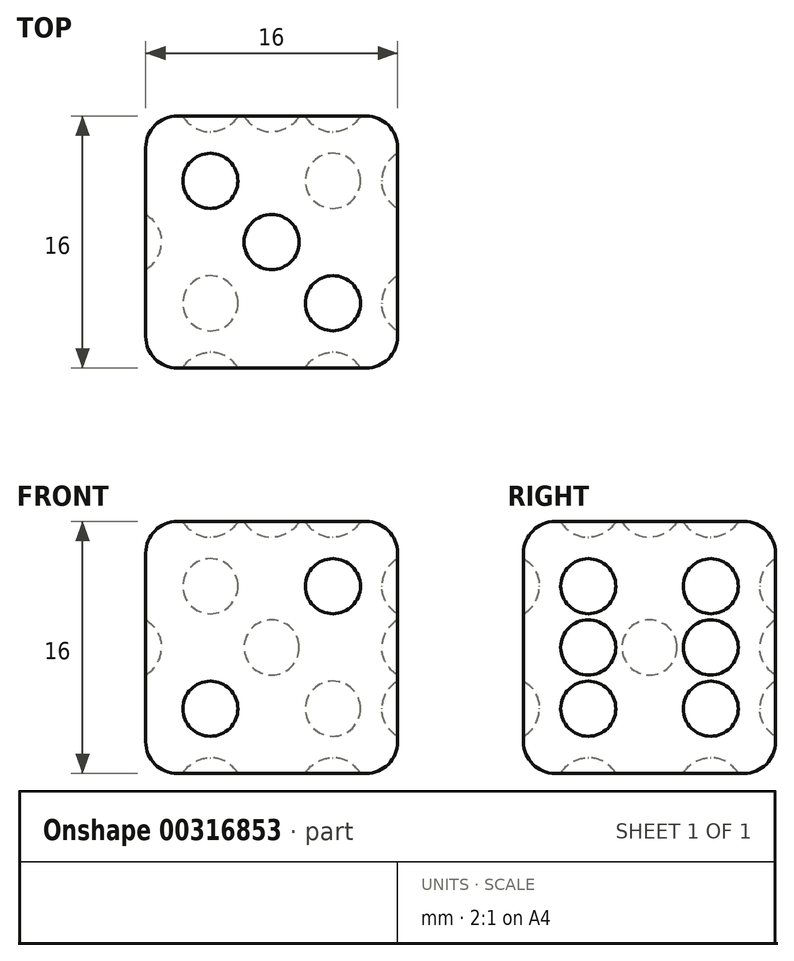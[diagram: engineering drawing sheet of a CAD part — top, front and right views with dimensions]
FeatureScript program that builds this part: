
annotation { "Feature Type Name" : "Feature", "Feature Type Description" : "" }
export const myFeature = defineFeature(function(context is Context, id is Id, definition is map)
    precondition{}
    {
        {
            var Q0;
            Q0=qCreatedBy(makeId("Top.planeOp"),FACE);
            var sketch = newSketch(context, id + "F0", { "sketchPlane" : qUnion([Q0])});
            skLineSegment(sketch, "E0.bottom", {"start": v(-8, 8) * mm, "end": v(8, 8) * mm});
            skLineSegment(sketch, "E0.top", {"start": v(-8, -8) * mm, "end": v(8, -8) * mm});
            skLineSegment(sketch, "E0.left", {"start": v(-8, 8) * mm, "end": v(-8, -8) * mm});
            skLineSegment(sketch, "E0.right", {"start": v(8, 8) * mm, "end": v(8, -8) * mm});
            skPoint(sketch, "E0.middle", {"position": v(0, 0) * mm});
            skSolve(sketch);
        }
        {
            var Q0;
            Q0=makeQuery(id+"F0.imprint","IMPRINT",FACE,{"disambiguationData":[TD([[makeQuery(id+"F0.imprint","IMPRINT",EDGE,{"derivedFrom":sQuery(id+"F0.wireOp",EDGE,"E0.bottom")}),-1.0]])]});
            extrude(context, id + "F1", {"entities" : qUnion([Q0]), "oppositeDirection" : true, "depth" : 16 * mm});
        }
        {
            var Q0;
            Q0=makeQuery(id+"F1.opExtrude","CAP_EDGE",EDGE,{"disambiguationData":[OSD([sQuery(id+"F0.wireOp",EDGE,"E0.top")])],"isStart":true});
            var Q1;
            Q1=makeQuery(id+"F1.opExtrude","CAP_EDGE",EDGE,{"disambiguationData":[OSD([sQuery(id+"F0.wireOp",EDGE,"E0.left")])],"isStart":true});
            var Q2;
            Q2=makeQuery(id+"F1.opExtrude","CAP_EDGE",EDGE,{"disambiguationData":[OSD([sQuery(id+"F0.wireOp",EDGE,"E0.bottom")])],"isStart":true});
            var Q3;
            Q3=makeQuery(id+"F1.opExtrude","CAP_EDGE",EDGE,{"disambiguationData":[OSD([sQuery(id+"F0.wireOp",EDGE,"E0.right")])],"isStart":true});
            var Q4;
            Q4=makeQuery(id+"F1.opExtrude","SWEPT_EDGE",EDGE,{"disambiguationData":[OSD([sQuery(id+"F0.wireOp",EDGE,"E0.top"),sQuery(id+"F0.wireOp",EDGE,"E0.right")])]});
            var Q5;
            Q5=makeQuery(id+"F1.opExtrude","SWEPT_EDGE",EDGE,{"disambiguationData":[OSD([sQuery(id+"F0.wireOp",EDGE,"E0.bottom"),sQuery(id+"F0.wireOp",EDGE,"E0.right")])]});
            var Q6;
            Q6=makeQuery(id+"F1.opExtrude","CAP_EDGE",EDGE,{"disambiguationData":[OSD([sQuery(id+"F0.wireOp",EDGE,"E0.right")])],"isStart":false});
            var Q7;
            Q7=makeQuery(id+"F1.opExtrude","CAP_EDGE",EDGE,{"disambiguationData":[OSD([sQuery(id+"F0.wireOp",EDGE,"E0.bottom")])],"isStart":false});
            var Q8;
            Q8=makeQuery(id+"F1.opExtrude","SWEPT_EDGE",EDGE,{"disambiguationData":[OSD([sQuery(id+"F0.wireOp",EDGE,"E0.bottom"),sQuery(id+"F0.wireOp",EDGE,"E0.left")])]});
            var Q9;
            Q9=makeQuery(id+"F1.opExtrude","CAP_EDGE",EDGE,{"disambiguationData":[OSD([sQuery(id+"F0.wireOp",EDGE,"E0.left")])],"isStart":false});
            var Q10;
            Q10=makeQuery(id+"F1.opExtrude","SWEPT_EDGE",EDGE,{"disambiguationData":[OSD([sQuery(id+"F0.wireOp",EDGE,"E0.top"),sQuery(id+"F0.wireOp",EDGE,"E0.left")])]});
            var Q11;
            Q11=makeQuery(id+"F1.opExtrude","CAP_EDGE",EDGE,{"disambiguationData":[OSD([sQuery(id+"F0.wireOp",EDGE,"E0.top")])],"isStart":false});
            var Q12;
            Q12=makeQuery(id+"F1.opExtrude","SWEPT_FACE",FACE,{"disambiguationData":[OSD([sQuery(id+"F0.wireOp",EDGE,"E0.bottom")])]});
            fillet(context, id + "F2", {"entities" : qUnion([Q0, Q1, Q2, Q3, Q4, Q5, Q6, Q7, Q8, Q9, Q10, Q11, Q12]), "radius" : 2 * mm, "tangentPropagation" : true, "allowEdgeOverflow" : false});
        }
        {
            var Q0;
            Q0=makeQuery(id+"F1.opExtrude","CAP_FACE",FACE,{"disambiguationData":[OSD([sQuery(id+"F0.wireOp",EDGE,"E0.bottom"),sQuery(id+"F0.wireOp",EDGE,"E0.top"),sQuery(id+"F0.wireOp",EDGE,"E0.left"),sQuery(id+"F0.wireOp",EDGE,"E0.right")])],"isStart":true});
            var sketch = newSketch(context, id + "F3", { "sketchPlane" : qUnion([Q0])});
            skCircle(sketch, "E1", {"center": v(0, 0) * mm, "radius": 1.75 * mm});
            skCircle(sketch, "E2", {"center": v(3.89, -3.89) * mm, "radius": 1.75 * mm});
            skPoint(sketch, "E2.second.point", {"position": v(3.96, -5.64) * mm});
            skCircle(sketch, "E3", {"center": v(-3.9, 3.89) * mm, "radius": 1.75 * mm});
            skPoint(sketch, "E3.third.point", {"position": v(-4.7, 2.34) * mm});
            skSolve(sketch);
        }
        {
            var Q0;
            Q0 = qSketchRegion(id + "F3", true);
            extrude(context, id + "F4", {"entities" : qUnion([Q0]), "operationType" : NewBodyOperationType.REMOVE, "oppositeDirection" : true, "depth" : 1 * mm});
        }
        {
            var Q0;
            Q0=makeQuery(id+"F4.boolean.opBoolean","COPY",EDGE,{"derivedFrom":makeQuery(id+"F4.opExtrude","CAP_EDGE",EDGE,{"disambiguationData":[OSD([sQuery(id+"F3.wireOp",EDGE,"E2")])],"isStart":false})});
            fillet(context, id + "F5", {"entities" : qUnion([Q0]), "radius" : 2.02 * mm, "tangentPropagation" : true, "allowEdgeOverflow" : false});
        }
        {
            var Q0;
            Q0=makeQuery(id+"F4.boolean.opBoolean","COPY",EDGE,{"derivedFrom":makeQuery(id+"F4.opExtrude","CAP_EDGE",EDGE,{"disambiguationData":[OSD([sQuery(id+"F3.wireOp",EDGE,"E1")])],"isStart":false})});
            fillet(context, id + "F6", {"entities" : qUnion([Q0]), "radius" : 2.02 * mm, "tangentPropagation" : true, "allowEdgeOverflow" : false});
        }
        {
            var Q0;
            Q0=makeQuery(id+"F4.boolean.opBoolean","COPY",EDGE,{"derivedFrom":makeQuery(id+"F4.opExtrude","CAP_EDGE",EDGE,{"disambiguationData":[OSD([sQuery(id+"F3.wireOp",EDGE,"E3")])],"isStart":false})});
            fillet(context, id + "F7", {"entities" : qUnion([Q0]), "radius" : 2.02 * mm, "tangentPropagation" : true, "allowEdgeOverflow" : false});
        }
        {
            var Q0;
            Q0=makeQuery(id+"F1.opExtrude","CAP_FACE",FACE,{"disambiguationData":[OSD([sQuery(id+"F0.wireOp",EDGE,"E0.bottom"),sQuery(id+"F0.wireOp",EDGE,"E0.top"),sQuery(id+"F0.wireOp",EDGE,"E0.left"),sQuery(id+"F0.wireOp",EDGE,"E0.right")])],"isStart":false});
            var sketch = newSketch(context, id + "F8", { "sketchPlane" : qUnion([Q0])});
            skCircle(sketch, "E4", {"center": v(-3.89, 3.89) * mm, "radius": 1.75 * mm});
            skPoint(sketch, "E4.first.point", {"position": v(-3.7, 6) * mm});
            skPoint(sketch, "E4.second.point", {"position": v(-6, 4.92) * mm});
            skPoint(sketch, "E4.third.point", {"position": v(-2.95, 2.41) * mm});
            skCircle(sketch, "E5", {"center": v(3.89, 3.89) * mm, "radius": 1.75 * mm});
            skPoint(sketch, "E5.third.point", {"position": v(3.84, 2.14) * mm});
            skCircle(sketch, "E6", {"center": v(-3.89, -3.89) * mm, "radius": 1.75 * mm});
            skPoint(sketch, "E6.third.point", {"position": v(-2.26, -3.26) * mm});
            skCircle(sketch, "E7", {"center": v(3.89, -3.89) * mm, "radius": 1.75 * mm});
            skSolve(sketch);
        }
        {
            var Q0;
            Q0 = qSketchRegion(id + "F8", true);
            extrude(context, id + "F9", {"entities" : qUnion([Q0]), "operationType" : NewBodyOperationType.REMOVE, "oppositeDirection" : true, "depth" : 1 * mm});
        }
        {
            var Q0;
            Q0=makeQuery(id+"F9.boolean.opBoolean","COPY",FACE,{"derivedFrom":makeQuery(id+"F9.opExtrude","CAP_FACE",FACE,{"disambiguationData":[OSD([sQuery(id+"F8.wireOp",EDGE,"E4")])],"isStart":false})});
            var Q1;
            Q1=makeQuery(id+"F9.boolean.opBoolean","COPY",FACE,{"derivedFrom":makeQuery(id+"F9.opExtrude","CAP_FACE",FACE,{"disambiguationData":[OSD([sQuery(id+"F8.wireOp",EDGE,"E5")])],"isStart":false})});
            var Q2;
            Q2=makeQuery(id+"F9.boolean.opBoolean","COPY",FACE,{"derivedFrom":makeQuery(id+"F9.opExtrude","CAP_FACE",FACE,{"disambiguationData":[OSD([sQuery(id+"F8.wireOp",EDGE,"E6")])],"isStart":false})});
            var Q3;
            Q3=makeQuery(id+"F9.boolean.opBoolean","COPY",FACE,{"derivedFrom":makeQuery(id+"F9.opExtrude","CAP_FACE",FACE,{"disambiguationData":[OSD([sQuery(id+"F8.wireOp",EDGE,"E7")])],"isStart":false})});
            fillet(context, id + "F10", {"entities" : qUnion([Q0, Q1, Q2, Q3]), "radius" : 2.02 * mm, "tangentPropagation" : true, "allowEdgeOverflow" : false});
        }
        {
            var Q0;
            Q0=makeQuery(id+"F1.opExtrude","SWEPT_FACE",FACE,{"disambiguationData":[OSD([sQuery(id+"F0.wireOp",EDGE,"E0.bottom")])]});
            var sketch = newSketch(context, id + "F11", { "sketchPlane" : qUnion([Q0])});
            skCircle(sketch, "E8", {"center": v(0, -8) * mm, "radius": 1.75 * mm});
            skCircle(sketch, "E9", {"center": v(-3.89, -4.1) * mm, "radius": 1.75 * mm});
            skCircle(sketch, "E10", {"center": v(-3.89, -11.89) * mm, "radius": 1.75 * mm});
            skCircle(sketch, "E11", {"center": v(3.89, -11.89) * mm, "radius": 1.75 * mm});
            skPoint(sketch, "E11.third.point", {"position": v(2.14, -11.8) * mm});
            skCircle(sketch, "E12", {"center": v(3.89, -4.11) * mm, "radius": 1.75 * mm});
            skPoint(sketch, "E12.third.point", {"position": v(2.9, -5.56) * mm});
            skSolve(sketch);
        }
        {
            var Q0;
            Q0 = qSketchRegion(id + "F11", true);
            extrude(context, id + "F12", {"entities" : qUnion([Q0]), "operationType" : NewBodyOperationType.REMOVE, "oppositeDirection" : true, "depth" : 1 * mm});
        }
        {
            var Q0;
            Q0=makeQuery(id+"F12.boolean.opBoolean","COPY",FACE,{"derivedFrom":makeQuery(id+"F12.opExtrude","CAP_FACE",FACE,{"disambiguationData":[OSD([sQuery(id+"F11.wireOp",EDGE,"E9")])],"isStart":false})});
            var Q1;
            Q1=makeQuery(id+"F12.boolean.opBoolean","COPY",FACE,{"derivedFrom":makeQuery(id+"F12.opExtrude","CAP_FACE",FACE,{"disambiguationData":[OSD([sQuery(id+"F11.wireOp",EDGE,"E8")])],"isStart":false})});
            var Q2;
            Q2=makeQuery(id+"F12.boolean.opBoolean","COPY",FACE,{"derivedFrom":makeQuery(id+"F12.opExtrude","CAP_FACE",FACE,{"disambiguationData":[OSD([sQuery(id+"F11.wireOp",EDGE,"E10")])],"isStart":false})});
            var Q3;
            Q3=makeQuery(id+"F12.boolean.opBoolean","COPY",FACE,{"derivedFrom":makeQuery(id+"F12.opExtrude","CAP_FACE",FACE,{"disambiguationData":[OSD([sQuery(id+"F11.wireOp",EDGE,"E11")])],"isStart":false})});
            var Q4;
            Q4=makeQuery(id+"F12.boolean.opBoolean","COPY",FACE,{"derivedFrom":makeQuery(id+"F12.opExtrude","CAP_FACE",FACE,{"disambiguationData":[OSD([sQuery(id+"F11.wireOp",EDGE,"E12")])],"isStart":false})});
            fillet(context, id + "F13", {"entities" : qUnion([Q0, Q1, Q2, Q3, Q4]), "radius" : 2.02 * mm, "tangentPropagation" : true, "allowEdgeOverflow" : false});
        }
        {
            var Q0;
            Q0=makeQuery(id+"F1.opExtrude","SWEPT_FACE",FACE,{"disambiguationData":[OSD([sQuery(id+"F0.wireOp",EDGE,"E0.right")])]});
            var sketch = newSketch(context, id + "F14", { "sketchPlane" : qUnion([Q0])});
            skCircle(sketch, "E13", {"center": v(3.9, -4.11) * mm, "radius": 1.75 * mm});
            skCircle(sketch, "E14", {"center": v(3.9, -8) * mm, "radius": 1.75 * mm});
            skCircle(sketch, "E15", {"center": v(3.9, -11.9) * mm, "radius": 1.75 * mm});
            skCircle(sketch, "E16.MirrorC", {"center": v(-3.89, -8) * mm, "radius": 1.75 * mm});
            skCircle(sketch, "E17.MirrorC", {"center": v(-3.89, -4.11) * mm, "radius": 1.75 * mm});
            skCircle(sketch, "E18.MirrorC", {"center": v(-3.89, -11.9) * mm, "radius": 1.75 * mm});
            skSolve(sketch);
        }
        {
            var Q0;
            Q0 = qSketchRegion(id + "F14", true);
            extrude(context, id + "F15", {"entities" : qUnion([Q0]), "operationType" : NewBodyOperationType.REMOVE, "oppositeDirection" : true, "depth" : 1 * mm});
        }
        {
            var Q0;
            Q0=makeQuery(id+"F15.boolean.opBoolean","COPY",FACE,{"derivedFrom":makeQuery(id+"F15.opExtrude","CAP_FACE",FACE,{"disambiguationData":[OSD([sQuery(id+"F14.wireOp",EDGE,"E18.MirrorC")])],"isStart":false})});
            var Q1;
            Q1=makeQuery(id+"F15.boolean.opBoolean","COPY",FACE,{"derivedFrom":makeQuery(id+"F15.opExtrude","CAP_FACE",FACE,{"disambiguationData":[OSD([sQuery(id+"F14.wireOp",EDGE,"E16.MirrorC")])],"isStart":false})});
            var Q2;
            Q2=makeQuery(id+"F15.boolean.opBoolean","COPY",FACE,{"derivedFrom":makeQuery(id+"F15.opExtrude","CAP_FACE",FACE,{"disambiguationData":[OSD([sQuery(id+"F14.wireOp",EDGE,"E17.MirrorC")])],"isStart":false})});
            var Q3;
            Q3=makeQuery(id+"F15.boolean.opBoolean","COPY",FACE,{"derivedFrom":makeQuery(id+"F15.opExtrude","CAP_FACE",FACE,{"disambiguationData":[OSD([sQuery(id+"F14.wireOp",EDGE,"E14")])],"isStart":false})});
            var Q4;
            Q4=makeQuery(id+"F15.boolean.opBoolean","COPY",FACE,{"derivedFrom":makeQuery(id+"F15.opExtrude","CAP_FACE",FACE,{"disambiguationData":[OSD([sQuery(id+"F14.wireOp",EDGE,"E15")])],"isStart":false})});
            var Q5;
            Q5=makeQuery(id+"F15.boolean.opBoolean","COPY",FACE,{"derivedFrom":makeQuery(id+"F15.opExtrude","CAP_FACE",FACE,{"disambiguationData":[OSD([sQuery(id+"F14.wireOp",EDGE,"E13")])],"isStart":false})});
            fillet(context, id + "F16", {"entities" : qUnion([Q0, Q1, Q2, Q3, Q4, Q5]), "radius" : 2.02 * mm, "tangentPropagation" : true, "allowEdgeOverflow" : false});
        }
        {
            var Q0;
            Q0=makeQuery(id+"F1.opExtrude","SWEPT_FACE",FACE,{"disambiguationData":[OSD([sQuery(id+"F0.wireOp",EDGE,"E0.left")])]});
            var sketch = newSketch(context, id + "F17", { "sketchPlane" : qUnion([Q0])});
            skCircle(sketch, "E19", {"center": v(0, -8) * mm, "radius": 1.75 * mm});
            skSolve(sketch);
        }
        {
            var Q0;
            Q0 = qSketchRegion(id + "F17", true);
            extrude(context, id + "F18", {"entities" : qUnion([Q0]), "operationType" : NewBodyOperationType.REMOVE, "oppositeDirection" : true, "depth" : 1 * mm});
        }
        {
            var Q0;
            Q0=makeQuery(id+"F18.boolean.opBoolean","COPY",FACE,{"derivedFrom":makeQuery(id+"F18.opExtrude","CAP_FACE",FACE,{"disambiguationData":[OSD([sQuery(id+"F17.wireOp",EDGE,"E19")])],"isStart":false})});
            fillet(context, id + "F19", {"entities" : qUnion([Q0]), "radius" : 2.02 * mm, "tangentPropagation" : true, "allowEdgeOverflow" : false});
        }
        {
            var Q0;
            Q0=makeQuery(id+"F1.opExtrude","SWEPT_FACE",FACE,{"disambiguationData":[OSD([sQuery(id+"F0.wireOp",EDGE,"E0.top")])]});
            var sketch = newSketch(context, id + "F20", { "sketchPlane" : qUnion([Q0])});
            skCircle(sketch, "E20", {"center": v(-3.9, -11.9) * mm, "radius": 1.75 * mm});
            skCircle(sketch, "E21", {"center": v(3.89, -4.11) * mm, "radius": 1.75 * mm});
            skSolve(sketch);
        }
        {
            var Q0;
            Q0 = qSketchRegion(id + "F20", true);
            extrude(context, id + "F21", {"entities" : qUnion([Q0]), "operationType" : NewBodyOperationType.REMOVE, "oppositeDirection" : true, "depth" : 1 * mm});
        }
        {
            var Q0;
            Q0=makeQuery(id+"F21.boolean.opBoolean","COPY",FACE,{"derivedFrom":makeQuery(id+"F21.opExtrude","CAP_FACE",FACE,{"disambiguationData":[OSD([sQuery(id+"F20.wireOp",EDGE,"E20")])],"isStart":false})});
            var Q1;
            Q1=makeQuery(id+"F21.boolean.opBoolean","COPY",FACE,{"derivedFrom":makeQuery(id+"F21.opExtrude","CAP_FACE",FACE,{"disambiguationData":[OSD([sQuery(id+"F20.wireOp",EDGE,"E21")])],"isStart":false})});
            fillet(context, id + "F22", {"entities" : qUnion([Q0, Q1]), "radius" : 2.02 * mm, "tangentPropagation" : true, "allowEdgeOverflow" : false});
        }
    });
